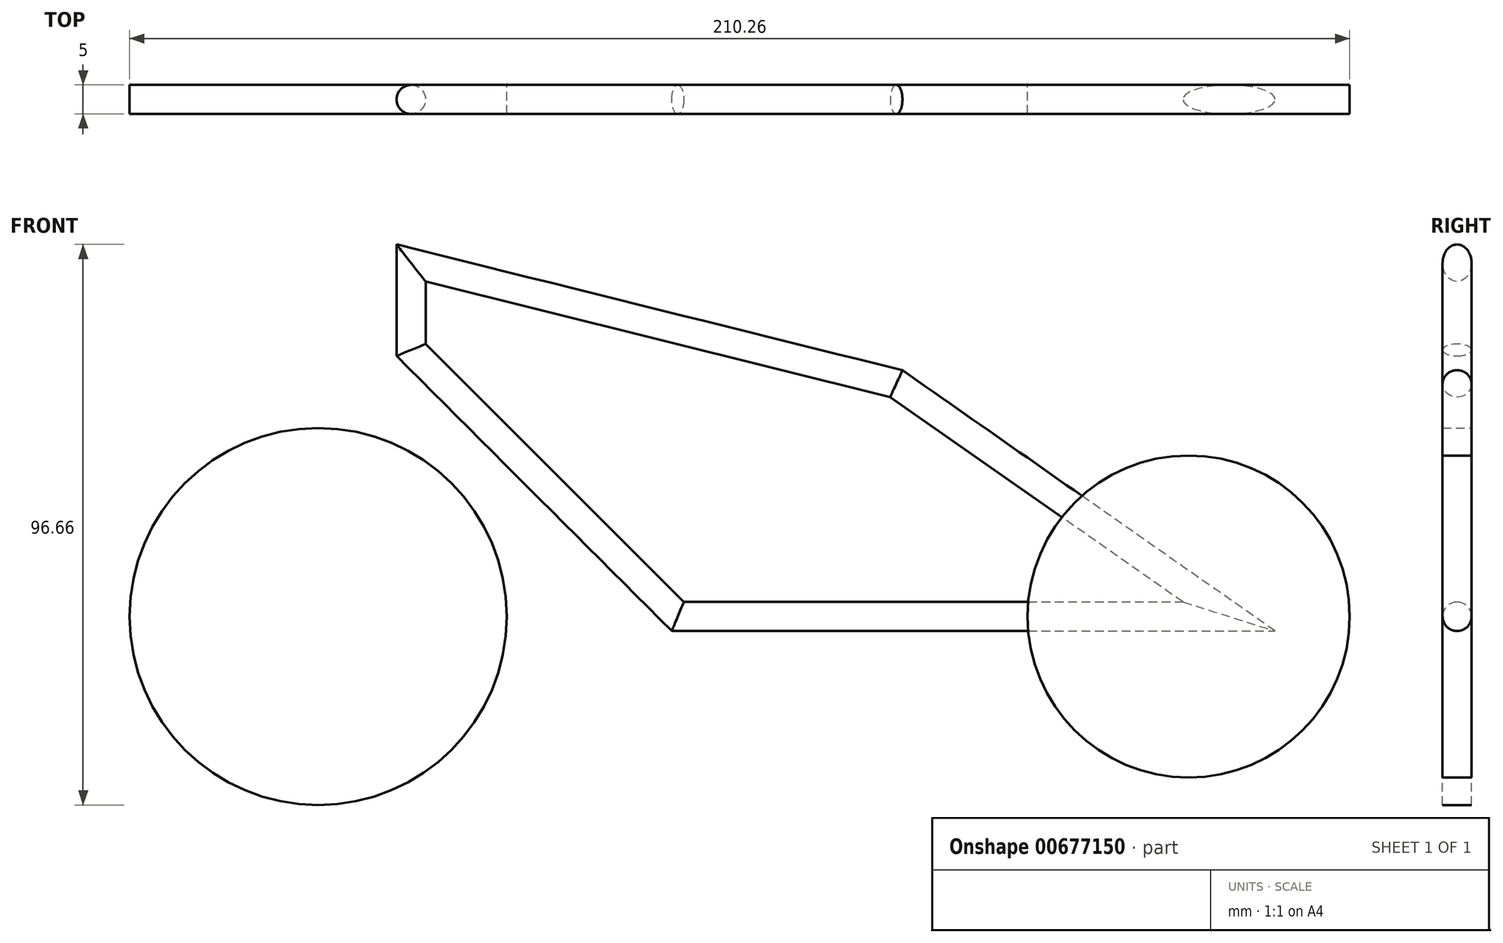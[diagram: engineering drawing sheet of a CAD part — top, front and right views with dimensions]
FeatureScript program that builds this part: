
annotation { "Feature Type Name" : "Feature", "Feature Type Description" : "" }
export const myFeature = defineFeature(function(context is Context, id is Id, definition is map)
    precondition{}
    {
        {
            var Q0;
            Q0=qCreatedBy(makeId("Front.planeOp"),FACE);
            var sketch = newSketch(context, id + "F0", { "sketchPlane" : qUnion([Q0])});
            skCircle(sketch, "E0", {"center": v(70, 0) * mm, "radius": 27.76 * mm});
            skCircle(sketch, "E1", {"center": v(-80, 0) * mm, "radius": 32.5 * mm});
            skSolve(sketch);
        }
        {
            var Q0;
            Q0=makeQuery(id+"F0.imprint","IMPRINT",FACE,{"disambiguationData":[TD([[makeQuery(id+"F0.imprint","IMPRINT",EDGE,{"derivedFrom":sQuery(id+"F0.wireOp",EDGE,"E0")}),1.0]])]});
            var Q1;
            Q1=makeQuery(id+"F0.imprint","IMPRINT",FACE,{"disambiguationData":[TD([[makeQuery(id+"F0.imprint","IMPRINT",EDGE,{"derivedFrom":sQuery(id+"F0.wireOp",EDGE,"E1")}),1.0]])]});
            extrude(context, id + "F1", {"entities" : qUnion([Q0, Q1]), "endBound" : BoundingType.SYMMETRIC, "depth" : 5 * mm, "offsetDistance" : 25 * mm});
        }
        {
            var Q0;
            Q0=qCreatedBy(makeId("Front.planeOp"),FACE);
            var sketch = newSketch(context, id + "F2", { "sketchPlane" : qUnion([Q0])});
            skLineSegment(sketch, "E2", {"start": v(-18.03, 0) * mm, "end": v(-64, 45.96) * mm});
            skLineSegment(sketch, "E3", {"start": v(-64, 45.96) * mm, "end": v(-64, 60.96) * mm});
            skLineSegment(sketch, "E4", {"start": v(-64, 60.96) * mm, "end": v(19.63, 40.15) * mm});
            skLineSegment(sketch, "E5", {"start": v(19.63, 40.15) * mm, "end": v(76.97, 0) * mm});
            skLineSegment(sketch, "E6", {"start": v(76.97, 0) * mm, "end": v(-18.03, 0) * mm});
            skSolve(sketch);
        }
        {
            var Q0;
            Q0=qCreatedBy(makeId("Right.planeOp"),FACE);
            var sketch = newSketch(context, id + "F3", { "sketchPlane" : qUnion([Q0])});
            skCircle(sketch, "E7", {"center": v(0, 0) * mm, "radius": 2.5 * mm});
            skSolve(sketch);
        }
        {
            var Q0;
            Q0=makeQuery(id+"F3.imprint","IMPRINT",FACE,{"disambiguationData":[TD([[makeQuery(id+"F3.imprint","IMPRINT",EDGE,{"derivedFrom":sQuery(id+"F3.wireOp",EDGE,"E7")}),1.0]])]});
            var Q1;
            Q1=sQuery(id+"F2.wireOp",EDGE,"E6");
            var Q2;
            Q2=sQuery(id+"F2.wireOp",EDGE,"E2");
            var Q3;
            Q3=sQuery(id+"F2.wireOp",EDGE,"E3");
            var Q4;
            Q4=sQuery(id+"F2.wireOp",EDGE,"E4");
            var Q5;
            Q5=sQuery(id+"F2.wireOp",EDGE,"E5");
            sweep(context, id + "F4", {"profiles" : qUnion([Q0]), "path" : qUnion([Q1, Q2, Q3, Q4, Q5])});
        }
    });
